# Revit family: Freestanding Tub Filler_TOTO_TBG02306
name_source: partatom
category: 衛生器具
revit_build: Autodesk Revit 2018 (Build: 20170223_1515(x64)
units: mm (PartAtom-declared; Revit-internal decimal feet)

## family parameters
OmniClass タイトル = Sanitary, Laundry, and Cleaning Equipment
OmniClass 番号 = 23.45.00.00
パーツ タイプ = 標準
ロード時にボイドで切り取り = いいえ
丸型コネクタ寸法 = 直径を使用
作業面ベース = いいえ
共有 = いいえ
常に垂直 = はい
部屋計算ポイント = いいえ

## types (1)
- Freestanding Tub Filler_TOTO_TBG02306
    Finish = faucet_material
    Height = 876
    Length = 378  [stored 1.24016 ft]
    TOTO AsiaOceania = TBG02306A
    TOTO AsiaOceania URL = http://asia.toto.com
    TOTO China = TBG02306B
    TOTO China URL = http://www.toto.com.cn
    TOTO HongKong = TBG02306B
    TOTO HongKong URL = http://hk.toto.com
    TOTO India = TBG02306A
    TOTO India URL = https://in.toto.com
    TOTO Korea = TBG02306B
    TOTO Korea URL = https://kr.toto.com
    TOTO Taiwan = TBG02306P
    TOTO Taiwan URL = https://www.twtoto.com.tw
    TOTO Thailand = TBG02306T
    TOTO Thailand URL = https://th.toto.com
    TOTO USA = TBG02306U
    TOTO USA URL = https://www.totousa.com
    TOTO Vietnam = TBG02306B
    TOTO Vietnam URL = https://vn.toto.com
    Width = 150.1
    タイプの説明 = Required Freestanding Tub Filler Base(TBN01105B)/水嘴固定配件(TBN01105B)需另购/*TOTO USA:TBN01105U
    モデル = TBG02306
    製造元 = TOTO Ltd.
    説明 = Freestanding Tub Filler/立式单柄双控浴缸水嘴(带手持花洒)

note: [stored X ft] marks values corroborated as IEEE doubles in the binary element streams (Revit-internal decimal feet)

## geometry (parser evidence)
native form markers: Sweep x2
no freeform markers — native parametric forms only
